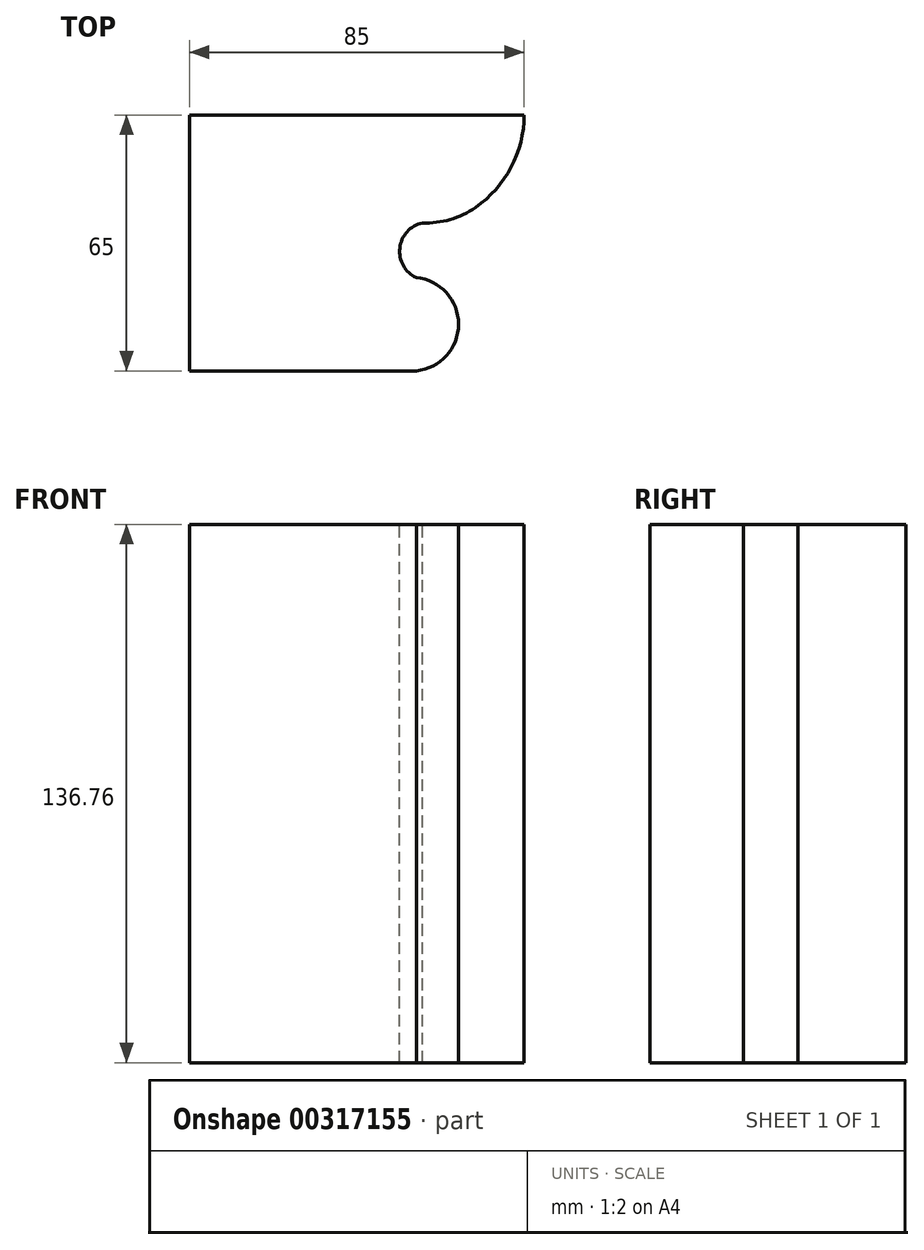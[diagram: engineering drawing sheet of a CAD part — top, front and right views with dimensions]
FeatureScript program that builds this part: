
annotation { "Feature Type Name" : "Feature", "Feature Type Description" : "" }
export const myFeature = defineFeature(function(context is Context, id is Id, definition is map)
    precondition{}
    {
        {
            var Q0;
            Q0=qCreatedBy(makeId("Front.planeOp"),FACE);
            var sketch = newSketch(context, id + "F0", { "sketchPlane" : qUnion([Q0])});
            skLineSegment(sketch, "E0.bottom", {"start": v(42.5, 68.38) * mm, "end": v(-42.5, 68.38) * mm});
            skLineSegment(sketch, "E0.top", {"start": v(42.5, -68.37) * mm, "end": v(-42.5, -68.37) * mm});
            skLineSegment(sketch, "E0.left", {"start": v(42.5, 68.38) * mm, "end": v(42.5, -68.37) * mm});
            skLineSegment(sketch, "E0.right", {"start": v(-42.5, 68.38) * mm, "end": v(-42.5, -68.37) * mm});
            skPoint(sketch, "E0.middle", {"position": v(0, 0) * mm});
            skSolve(sketch);
        }
        {
            var Q0;
            Q0 = qSketchRegion(id + "F0", true);
            extrude(context, id + "F1", {"entities" : qUnion([Q0]), "depth" : 65 * mm});
        }
        {
            var Q0;
            Q0=makeQuery(id+"F1.opExtrude","SWEPT_FACE",FACE,{"disambiguationData":[OSD([sQuery(id+"F0.wireOp",EDGE,"E0.bottom")])]});
            var sketch = newSketch(context, id + "F2", { "sketchPlane" : qUnion([Q0])});
            skArc(sketch, "E1", {"start": v(30.14, -23.46) * mm, "mid": v(39.22, -13.26) * mm, "end": v(42.5, 0) * mm});
            skArc(sketch, "E2", {"start": v(16.65, -27.4) * mm, "mid": v(23.72, -26.54) * mm, "end": v(30.14, -23.46) * mm});
            skArc(sketch, "E3", {"start": v(16.65, -27.4) * mm, "mid": v(10.93, -33.8) * mm, "end": v(15.1, -41.3) * mm});
            skArc(sketch, "E4", {"start": v(15.1, -65) * mm, "mid": v(25.83, -53.15) * mm, "end": v(15.1, -41.3) * mm});
            skLineSegment(sketch, "E5", {"start": v(15.1, -65) * mm, "end": v(42.5, -65) * mm});
            skLineSegment(sketch, "E6", {"start": v(42.5, -65) * mm, "end": v(42.5, 0) * mm});
            skSolve(sketch);
        }
        {
            var Q0;
            Q0 = qSketchRegion(id + "F2", true);
            extrude(context, id + "F3", {"entities" : qUnion([Q0]), "operationType" : NewBodyOperationType.REMOVE, "oppositeDirection" : true, "depth" : 200 * mm});
        }
    });
